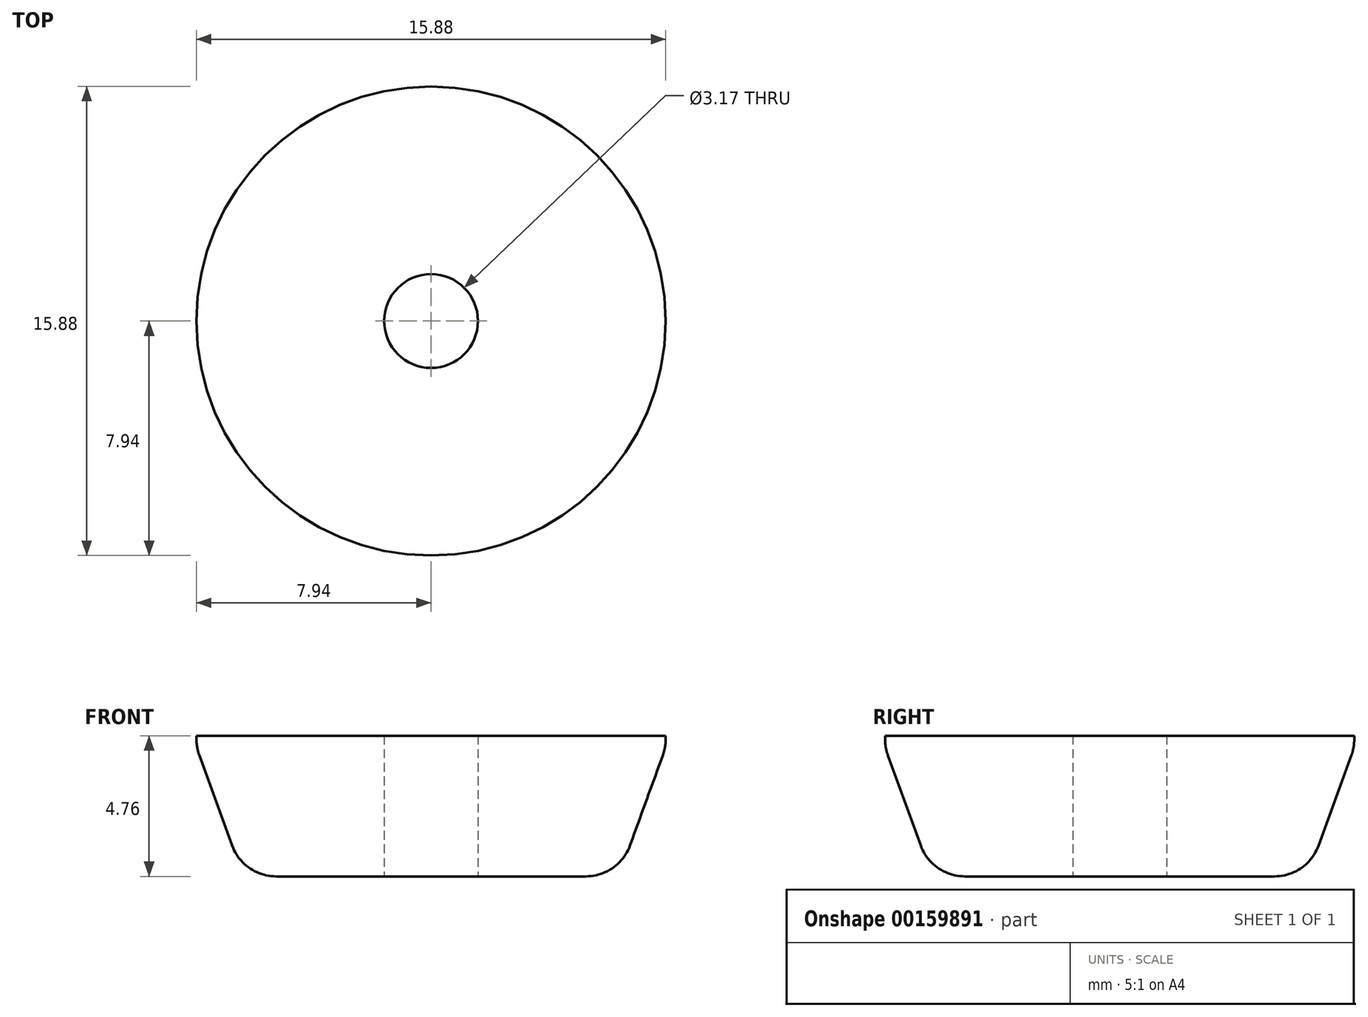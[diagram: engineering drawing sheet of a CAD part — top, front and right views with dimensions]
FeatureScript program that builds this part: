
annotation { "Feature Type Name" : "Feature", "Feature Type Description" : "" }
export const myFeature = defineFeature(function(context is Context, id is Id, definition is map)
    precondition{}
    {
        {
            var Q0;
            Q0=qCreatedBy(makeId("Front.planeOp"),FACE);
            var sketch = newSketch(context, id + "F0", { "sketchPlane" : qUnion([Q0])});
            skLineSegment(sketch, "E0.top", {"start": v(0, 12.7) * mm, "end": v(10.97, 12.7) * mm});
            skLineSegment(sketch, "E0.left", {"start": v(0, 0) * mm, "end": v(0, 12.7) * mm});
            skLineSegment(sketch, "E1", {"start": v(0, 0) * mm, "end": v(6.35, 0) * mm});
            skLineSegment(sketch, "E2", {"start": v(6.35, 0) * mm, "end": v(10.97, 12.7) * mm});
            skLineSegment(sketch, "E3", {"start": v(7.94, 12.7) * mm, "end": v(7.94, 4.36) * mm});
            skSolve(sketch);
        }
        {
            var Q0;
            {var subQ3=sQuery(id+"F0.wireOp",EDGE,"E0.left");Q0=makeQuery(id+"F0.imprint","IMPRINT",FACE,{"disambiguationData":[TD([[makeQuery(id+"F0.imprint","IMPRINT",EDGE,{"derivedFrom":subQ3}),-1.0]])]});}
            var Q1;
            Q1=sQuery(id+"F0.wireOp",EDGE,"E0.left");
            revolve(context, id + "F1", {"entities" : qUnion([Q0]), "axis" : qUnion([Q1]), "revolveType" : RevolveType.FULL});
        }
        {
            var Q0;
            Q0=makeQuery(id+"F1.opRevolve","SWEPT_EDGE",EDGE,{"disambiguationData":[OSD([sQuery(id+"F0.wireOp",EDGE,"E1"),sQuery(id+"F0.wireOp",EDGE,"E2")])]});
            var Q1;
            Q1=makeQuery(id+"F1.opRevolve","SWEPT_EDGE",EDGE,{"disambiguationData":[OSD([sQuery(id+"F0.wireOp",EDGE,"E2"),sQuery(id+"F0.wireOp",EDGE,"E3")])]});
            fillet(context, id + "F2", {"entities" : qUnion([Q0, Q1]), "radius" : 1.59 * mm, "tangentPropagation" : true, "allowEdgeOverflow" : false});
        }
        {
            var Q0;
            Q0=qCreatedBy(makeId("Front.planeOp"),FACE);
            var sketch = newSketch(context, id + "F3", { "sketchPlane" : qUnion([Q0])});
            skLineSegment(sketch, "E4.bottom", {"start": v(12.7, 4.76) * mm, "end": v(-12.7, 4.76) * mm});
            skLineSegment(sketch, "E4.top", {"start": v(12.7, 20.64) * mm, "end": v(-12.7, 20.64) * mm});
            skLineSegment(sketch, "E4.left", {"start": v(12.7, 4.76) * mm, "end": v(12.7, 20.64) * mm});
            skLineSegment(sketch, "E4.right", {"start": v(-12.7, 4.76) * mm, "end": v(-12.7, 20.64) * mm});
            skPoint(sketch, "E4.middle", {"position": v(0, 12.7) * mm});
            skSolve(sketch);
        }
        {
            var Q0;
            Q0=makeQuery(id+"F3.imprint","IMPRINT",FACE,{"disambiguationData":[TD([[makeQuery(id+"F3.imprint","IMPRINT",EDGE,{"derivedFrom":sQuery(id+"F3.wireOp",EDGE,"E4.bottom")}),-1.0]])]});
            extrude(context, id + "F4", {"entities" : qUnion([Q0]), "operationType" : NewBodyOperationType.REMOVE, "endBound" : BoundingType.SYMMETRIC, "oppositeDirection" : true, "depth" : 25.4 * mm});
        }
        {
            var Q0;
            Q0=makeQuery(id+"F1.opRevolve","SWEPT_FACE",FACE,{"disambiguationData":[OSD([sQuery(id+"F0.wireOp",EDGE,"E1")])]});
            var sketch = newSketch(context, id + "F5", { "sketchPlane" : qUnion([Q0])});
            skPoint(sketch, "E5", {"position": v(0, 0) * mm});
            skSolve(sketch);
        }
        {
            var Q0;
            Q0=sQuery(id+"F5.wireOp",VERTEX,"E5");
            var Q1;
            Q1=makeQuery(id+"F1.opRevolve","SWEPT_BODY",BODY,{"disambiguationData":[OSD([sQuery(id+"F0.wireOp",EDGE,"E0.top"),sQuery(id+"F0.wireOp",EDGE,"E0.left"),sQuery(id+"F0.wireOp",EDGE,"E1"),sQuery(id+"F0.wireOp",EDGE,"E2"),sQuery(id+"F0.wireOp",EDGE,"E3")])]});
            hole(context, id + "F6", {"style" : HoleStyle.C_BORE, "endStyle" : HoleEndStyle.BLIND, "holeDiameter" : 1.59 * mm, "cBoreDiameter" : 3.17 * mm, "cBoreDepth" : 6.35 * mm, "holeDepth" : 19.05 * mm, "locations" : qUnion([Q0]), "scope" : qUnion([Q1])});
        }
    });
